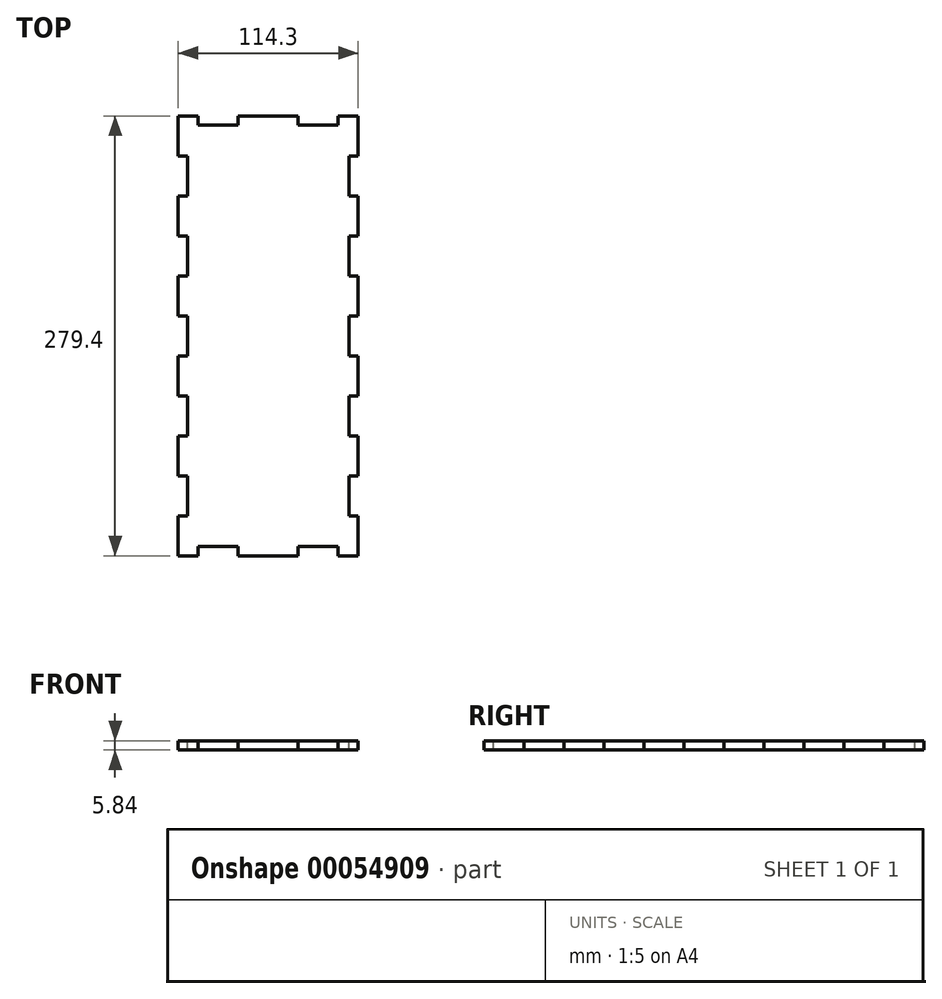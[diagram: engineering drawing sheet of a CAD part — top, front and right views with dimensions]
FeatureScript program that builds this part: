
annotation { "Feature Type Name" : "Feature", "Feature Type Description" : "" }
export const myFeature = defineFeature(function(context is Context, id is Id, definition is map)
    precondition{}
    {
        {
            var Q0;
            Q0=qCreatedBy(makeId("Top.planeOp"),FACE);
            var sketch = newSketch(context, id + "F0", { "sketchPlane" : qUnion([Q0])});
            skLineSegment(sketch, "E0.bottom", {"start": v(-60.45, -96.69) * mm, "end": v(53.85, -96.69) * mm});
            skLineSegment(sketch, "E0.top", {"start": v(-60.45, 182.71) * mm, "end": v(53.85, 182.71) * mm});
            skLineSegment(sketch, "E0.left", {"start": v(-60.45, -96.69) * mm, "end": v(-60.45, 182.71) * mm});
            skLineSegment(sketch, "E0.right", {"start": v(53.85, -96.69) * mm, "end": v(53.85, 182.71) * mm});
            skSolve(sketch);
        }
        {
            var Q0;
            Q0=makeQuery(id+"F0.imprint","IMPRINT",FACE,{"disambiguationData":[TD([[makeQuery(id+"F0.imprint","IMPRINT",EDGE,{"derivedFrom":sQuery(id+"F0.wireOp",EDGE,"E0.bottom")}),1.0]])]});
            extrude(context, id + "F1", {"entities" : qUnion([Q0]), "depth" : 5.84 * mm});
        }
        {
            var Q0;
            Q0=makeQuery(id+"F1.opExtrude","CAP_FACE",FACE,{"disambiguationData":[OSD([sQuery(id+"F0.wireOp",EDGE,"E0.bottom"),sQuery(id+"F0.wireOp",EDGE,"E0.top"),sQuery(id+"F0.wireOp",EDGE,"E0.left"),sQuery(id+"F0.wireOp",EDGE,"E0.right")])],"isStart":false});
            var sketch = newSketch(context, id + "F2", { "sketchPlane" : qUnion([Q0])});
            skLineSegment(sketch, "E1.bottom", {"start": v(-47.75, -96.69) * mm, "end": v(-22.35, -96.69) * mm});
            skLineSegment(sketch, "E1.top", {"start": v(-47.75, -90.84) * mm, "end": v(-22.35, -90.84) * mm});
            skLineSegment(sketch, "E1.left", {"start": v(-47.75, -96.69) * mm, "end": v(-47.75, -90.84) * mm});
            skLineSegment(sketch, "E1.right", {"start": v(-22.35, -96.69) * mm, "end": v(-22.35, -90.84) * mm});
            skLineSegment(sketch, "E2.bottom", {"start": v(41.15, -96.69) * mm, "end": v(15.75, -96.69) * mm});
            skLineSegment(sketch, "E2.top", {"start": v(41.15, -90.84) * mm, "end": v(15.75, -90.84) * mm});
            skLineSegment(sketch, "E2.left", {"start": v(41.15, -96.69) * mm, "end": v(41.15, -90.84) * mm});
            skLineSegment(sketch, "E2.right", {"start": v(15.75, -96.69) * mm, "end": v(15.75, -90.84) * mm});
            skLineSegment(sketch, "E3.bottom", {"start": v(-60.45, -71.29) * mm, "end": v(-54.6, -71.29) * mm});
            skLineSegment(sketch, "E3.top", {"start": v(-60.45, -45.89) * mm, "end": v(-54.6, -45.89) * mm});
            skLineSegment(sketch, "E3.left", {"start": v(-60.45, -71.29) * mm, "end": v(-60.45, -45.89) * mm});
            skLineSegment(sketch, "E3.right", {"start": v(-54.6, -71.29) * mm, "end": v(-54.6, -45.89) * mm});
            skLineSegment(sketch, "E4.bottom", {"start": v(-60.45, -20.49) * mm, "end": v(-54.6, -20.49) * mm});
            skLineSegment(sketch, "E4.top", {"start": v(-60.45, 4.91) * mm, "end": v(-54.6, 4.91) * mm});
            skLineSegment(sketch, "E4.left", {"start": v(-60.45, -20.49) * mm, "end": v(-60.45, 4.91) * mm});
            skLineSegment(sketch, "E4.right", {"start": v(-54.6, -20.49) * mm, "end": v(-54.6, 4.91) * mm});
            skLineSegment(sketch, "E5.bottom", {"start": v(-60.45, 30.31) * mm, "end": v(-54.6, 30.31) * mm});
            skLineSegment(sketch, "E5.top", {"start": v(-60.45, 55.71) * mm, "end": v(-54.6, 55.71) * mm});
            skLineSegment(sketch, "E5.left", {"start": v(-60.45, 30.31) * mm, "end": v(-60.45, 55.71) * mm});
            skLineSegment(sketch, "E5.right", {"start": v(-54.6, 30.31) * mm, "end": v(-54.6, 55.71) * mm});
            skLineSegment(sketch, "E6.bottom", {"start": v(-60.45, 81.11) * mm, "end": v(-54.6, 81.11) * mm});
            skLineSegment(sketch, "E6.top", {"start": v(-60.45, 106.51) * mm, "end": v(-54.6, 106.51) * mm});
            skLineSegment(sketch, "E6.left", {"start": v(-60.45, 81.11) * mm, "end": v(-60.45, 106.51) * mm});
            skLineSegment(sketch, "E6.right", {"start": v(-54.6, 81.11) * mm, "end": v(-54.6, 106.51) * mm});
            skLineSegment(sketch, "E7.bottom", {"start": v(53.85, -71.29) * mm, "end": v(48, -71.29) * mm});
            skLineSegment(sketch, "E7.top", {"start": v(53.85, -45.89) * mm, "end": v(48, -45.89) * mm});
            skLineSegment(sketch, "E7.left", {"start": v(53.85, -71.29) * mm, "end": v(53.85, -45.89) * mm});
            skLineSegment(sketch, "E7.right", {"start": v(48, -71.29) * mm, "end": v(48, -45.89) * mm});
            skLineSegment(sketch, "E8.bottom", {"start": v(53.85, 30.31) * mm, "end": v(48, 30.31) * mm});
            skLineSegment(sketch, "E8.top", {"start": v(53.85, 55.71) * mm, "end": v(48, 55.71) * mm});
            skLineSegment(sketch, "E8.left", {"start": v(53.85, 30.31) * mm, "end": v(53.85, 55.71) * mm});
            skLineSegment(sketch, "E8.right", {"start": v(48, 30.31) * mm, "end": v(48, 55.71) * mm});
            skLineSegment(sketch, "E9.bottom", {"start": v(53.85, 81.11) * mm, "end": v(48, 81.11) * mm});
            skLineSegment(sketch, "E9.top", {"start": v(53.85, 106.51) * mm, "end": v(48, 106.51) * mm});
            skLineSegment(sketch, "E9.left", {"start": v(53.85, 81.11) * mm, "end": v(53.85, 106.51) * mm});
            skLineSegment(sketch, "E9.right", {"start": v(48, 81.11) * mm, "end": v(48, 106.51) * mm});
            skLineSegment(sketch, "E10.bottom", {"start": v(53.85, -20.49) * mm, "end": v(48, -20.49) * mm});
            skLineSegment(sketch, "E10.top", {"start": v(53.85, 4.91) * mm, "end": v(48, 4.91) * mm});
            skLineSegment(sketch, "E10.left", {"start": v(53.85, -20.49) * mm, "end": v(53.85, 4.91) * mm});
            skLineSegment(sketch, "E10.right", {"start": v(48, -20.49) * mm, "end": v(48, 4.91) * mm});
            skLineSegment(sketch, "E11.bottom", {"start": v(-47.75, 182.71) * mm, "end": v(-22.35, 182.71) * mm});
            skLineSegment(sketch, "E11.top", {"start": v(-47.75, 176.87) * mm, "end": v(-22.35, 176.87) * mm});
            skLineSegment(sketch, "E11.left", {"start": v(-47.75, 182.71) * mm, "end": v(-47.75, 176.87) * mm});
            skLineSegment(sketch, "E11.right", {"start": v(-22.35, 182.71) * mm, "end": v(-22.35, 176.87) * mm});
            skLineSegment(sketch, "E12.bottom", {"start": v(15.75, 182.71) * mm, "end": v(41.15, 182.71) * mm});
            skLineSegment(sketch, "E12.top", {"start": v(15.75, 176.87) * mm, "end": v(41.15, 176.87) * mm});
            skLineSegment(sketch, "E12.left", {"start": v(15.75, 182.71) * mm, "end": v(15.75, 176.87) * mm});
            skLineSegment(sketch, "E12.right", {"start": v(41.15, 182.71) * mm, "end": v(41.15, 176.87) * mm});
            skLineSegment(sketch, "E13.bottom", {"start": v(-60.45, 131.91) * mm, "end": v(-54.6, 131.91) * mm});
            skLineSegment(sketch, "E13.top", {"start": v(-60.45, 157.31) * mm, "end": v(-54.6, 157.31) * mm});
            skLineSegment(sketch, "E13.left", {"start": v(-60.45, 131.91) * mm, "end": v(-60.45, 157.31) * mm});
            skLineSegment(sketch, "E13.right", {"start": v(-54.6, 131.91) * mm, "end": v(-54.6, 157.31) * mm});
            skLineSegment(sketch, "E14.bottom", {"start": v(53.85, 131.91) * mm, "end": v(48, 131.91) * mm});
            skLineSegment(sketch, "E14.top", {"start": v(53.85, 157.31) * mm, "end": v(48, 157.31) * mm});
            skLineSegment(sketch, "E14.left", {"start": v(53.85, 131.91) * mm, "end": v(53.85, 157.31) * mm});
            skLineSegment(sketch, "E14.right", {"start": v(48, 131.91) * mm, "end": v(48, 157.31) * mm});
            skSolve(sketch);
        }
        {
            var Q0;
            Q0=makeQuery(id+"F2.imprint","IMPRINT",FACE,{"disambiguationData":[TD([[makeQuery(id+"F2.imprint","IMPRINT",EDGE,{"derivedFrom":sQuery(id+"F2.wireOp",EDGE,"b2b58f17-ebd9-4283-9503-4e9880558bd8.bottom")}),-1.0]])]});
            var Q1;
            Q1=makeQuery(id+"F2.imprint","IMPRINT",FACE,{"disambiguationData":[TD([[makeQuery(id+"F2.imprint","IMPRINT",EDGE,{"derivedFrom":sQuery(id+"F2.wireOp",EDGE,"70042725-0dfb-4d17-823a-1ae248a78f88.bottom")}),-1.0]])]});
            var Q2;
            Q2=makeQuery(id+"F2.imprint","IMPRINT",FACE,{"disambiguationData":[TD([[makeQuery(id+"F2.imprint","IMPRINT",EDGE,{"derivedFrom":sQuery(id+"F2.wireOp",EDGE,"144aa9f8-8e5a-4397-9c6a-1dbfcf82a634.bottom")}),1.0]])]});
            var Q3;
            Q3=makeQuery(id+"F2.imprint","IMPRINT",FACE,{"disambiguationData":[TD([[makeQuery(id+"F2.imprint","IMPRINT",EDGE,{"derivedFrom":sQuery(id+"F2.wireOp",EDGE,"2c262388-56d7-4c32-bfca-3f3ff5ee4251.bottom")}),-1.0]])]});
            var Q4;
            Q4=makeQuery(id+"F2.imprint","IMPRINT",FACE,{"disambiguationData":[TD([[makeQuery(id+"F2.imprint","IMPRINT",EDGE,{"derivedFrom":sQuery(id+"F2.wireOp",EDGE,"E9.bottom")}),-1.0]])]});
            var Q5;
            Q5=makeQuery(id+"F2.imprint","IMPRINT",FACE,{"disambiguationData":[TD([[makeQuery(id+"F2.imprint","IMPRINT",EDGE,{"derivedFrom":sQuery(id+"F2.wireOp",EDGE,"E6.bottom")}),1.0]])]});
            var Q6;
            Q6=makeQuery(id+"F2.imprint","IMPRINT",FACE,{"disambiguationData":[TD([[makeQuery(id+"F2.imprint","IMPRINT",EDGE,{"derivedFrom":sQuery(id+"F2.wireOp",EDGE,"E5.bottom")}),1.0]])]});
            var Q7;
            Q7=makeQuery(id+"F2.imprint","IMPRINT",FACE,{"disambiguationData":[TD([[makeQuery(id+"F2.imprint","IMPRINT",EDGE,{"derivedFrom":sQuery(id+"F2.wireOp",EDGE,"E8.bottom")}),-1.0]])]});
            var Q8;
            Q8=makeQuery(id+"F2.imprint","IMPRINT",FACE,{"disambiguationData":[TD([[makeQuery(id+"F2.imprint","IMPRINT",EDGE,{"derivedFrom":sQuery(id+"F2.wireOp",EDGE,"E10.bottom")}),-1.0]])]});
            var Q9;
            Q9=makeQuery(id+"F2.imprint","IMPRINT",FACE,{"disambiguationData":[TD([[makeQuery(id+"F2.imprint","IMPRINT",EDGE,{"derivedFrom":sQuery(id+"F2.wireOp",EDGE,"E7.bottom")}),-1.0]])]});
            var Q10;
            Q10=makeQuery(id+"F2.imprint","IMPRINT",FACE,{"disambiguationData":[TD([[makeQuery(id+"F2.imprint","IMPRINT",EDGE,{"derivedFrom":sQuery(id+"F2.wireOp",EDGE,"E2.bottom")}),1.0]])]});
            var Q11;
            Q11=makeQuery(id+"F2.imprint","IMPRINT",FACE,{"disambiguationData":[TD([[makeQuery(id+"F2.imprint","IMPRINT",EDGE,{"derivedFrom":sQuery(id+"F2.wireOp",EDGE,"E1.bottom")}),1.0]])]});
            var Q12;
            Q12=makeQuery(id+"F2.imprint","IMPRINT",FACE,{"disambiguationData":[TD([[makeQuery(id+"F2.imprint","IMPRINT",EDGE,{"derivedFrom":sQuery(id+"F2.wireOp",EDGE,"E3.bottom")}),1.0]])]});
            var Q13;
            Q13=makeQuery(id+"F2.imprint","IMPRINT",FACE,{"disambiguationData":[TD([[makeQuery(id+"F2.imprint","IMPRINT",EDGE,{"derivedFrom":sQuery(id+"F2.wireOp",EDGE,"E4.bottom")}),1.0]])]});
            var Q14;
            Q14=makeQuery(id+"F2.imprint","IMPRINT",FACE,{"disambiguationData":[TD([[makeQuery(id+"F2.imprint","IMPRINT",EDGE,{"derivedFrom":sQuery(id+"F2.wireOp",EDGE,"E12.bottom")}),-1.0]])]});
            var Q15;
            Q15=makeQuery(id+"F2.imprint","IMPRINT",FACE,{"disambiguationData":[TD([[makeQuery(id+"F2.imprint","IMPRINT",EDGE,{"derivedFrom":sQuery(id+"F2.wireOp",EDGE,"E11.bottom")}),-1.0]])]});
            var Q16;
            Q16=makeQuery(id+"F2.imprint","IMPRINT",FACE,{"disambiguationData":[TD([[makeQuery(id+"F2.imprint","IMPRINT",EDGE,{"derivedFrom":sQuery(id+"F2.wireOp",EDGE,"E13.bottom")}),1.0]])]});
            var Q17;
            Q17=makeQuery(id+"F2.imprint","IMPRINT",FACE,{"disambiguationData":[TD([[makeQuery(id+"F2.imprint","IMPRINT",EDGE,{"derivedFrom":sQuery(id+"F2.wireOp",EDGE,"E14.bottom")}),-1.0]])]});
            var Q18;
            Q18=makeQuery(id+"F1.opExtrude","CAP_FACE",FACE,{"disambiguationData":[OSD([sQuery(id+"F0.wireOp",EDGE,"E0.bottom"),sQuery(id+"F0.wireOp",EDGE,"E0.top"),sQuery(id+"F0.wireOp",EDGE,"E0.left"),sQuery(id+"F0.wireOp",EDGE,"E0.right")])],"isStart":true});
            extrude(context, id + "F3", {"entities" : qUnion([Q0, Q1, Q2, Q3, Q4, Q5, Q6, Q7, Q8, Q9, Q10, Q11, Q12, Q13, Q14, Q15, Q16, Q17]), "operationType" : NewBodyOperationType.REMOVE, "endBound" : BoundingType.UP_TO_SURFACE, "oppositeDirection" : true, "endBoundEntityFace" : qUnion([Q18]), "depth" : 25.4 * mm});
        }
    });
